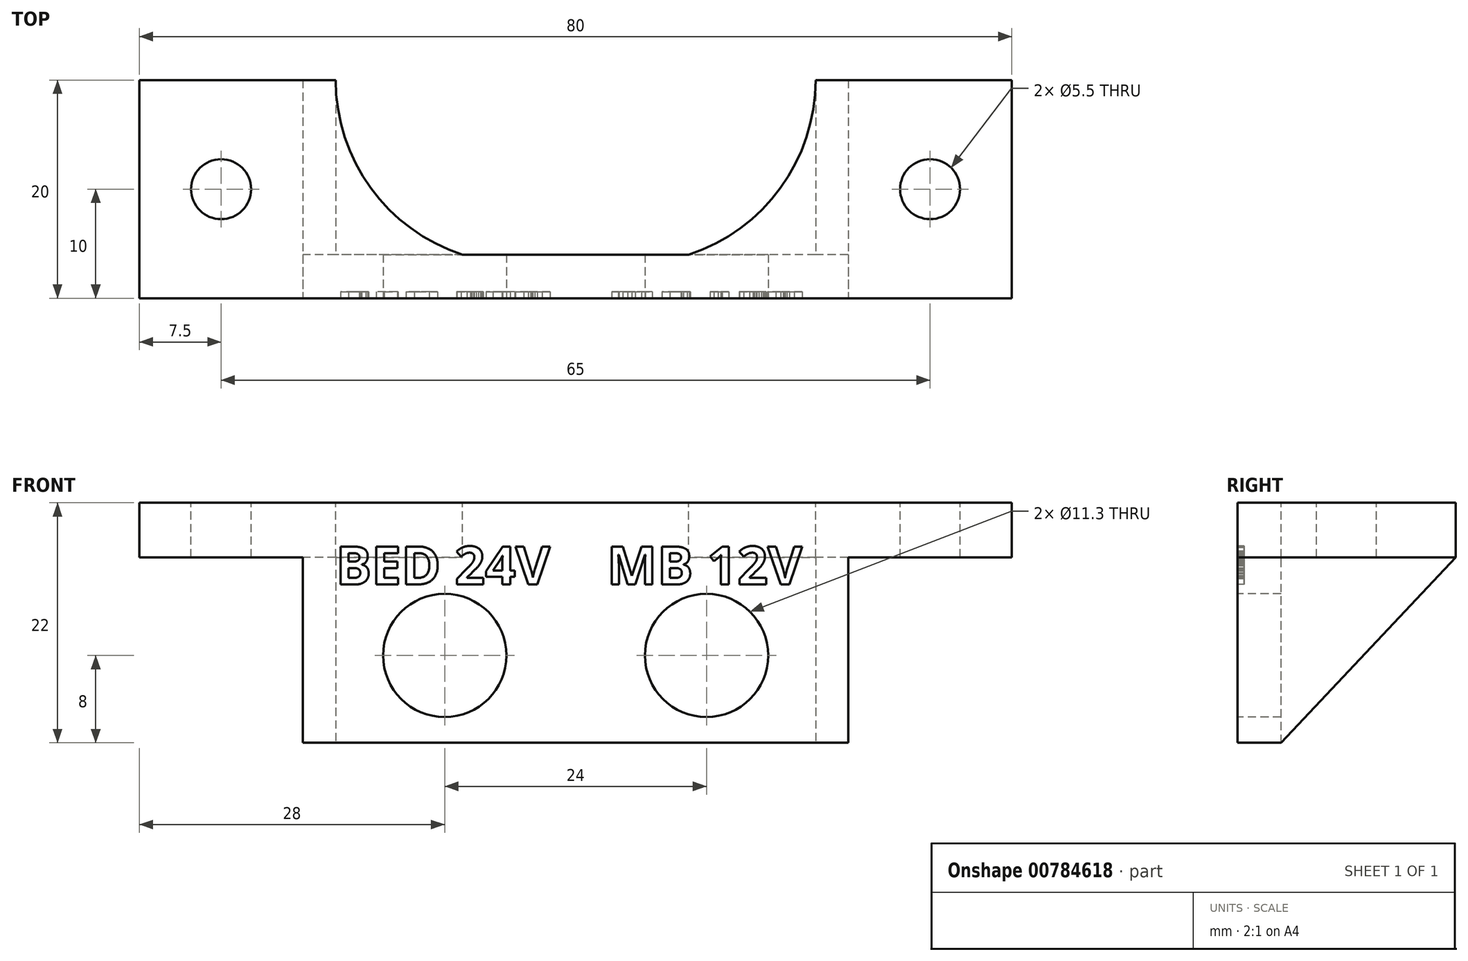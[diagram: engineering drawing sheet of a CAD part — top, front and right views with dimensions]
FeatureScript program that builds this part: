
annotation { "Feature Type Name" : "Feature", "Feature Type Description" : "" }
export const myFeature = defineFeature(function(context is Context, id is Id, definition is map)
    precondition{}
    {
        {
            var Q0;
            Q0=qCreatedBy(makeId("Front.planeOp"),FACE);
            var sketch = newSketch(context, id + "F0", { "sketchPlane" : qUnion([Q0])});
            skLineSegment(sketch, "E0.bottom", {"start": v(25, 11) * mm, "end": v(-25, 11) * mm});
            skLineSegment(sketch, "E0.top", {"start": v(25, -11) * mm, "end": v(-25, -11) * mm});
            skLineSegment(sketch, "E0.left", {"start": v(25, 11) * mm, "end": v(25, -11) * mm});
            skLineSegment(sketch, "E0.right", {"start": v(-25, 11) * mm, "end": v(-25, -11) * mm});
            skPoint(sketch, "E0.middle", {"position": v(0, 0) * mm});
            skCircle(sketch, "E1", {"center": v(-12, -3) * mm, "radius": 5.65 * mm});
            skCircle(sketch, "E2.MirrorC", {"center": v(12, -3) * mm, "radius": 5.65 * mm});
            skSolve(sketch);
        }
        {
            var Q0;
            Q0=qCreatedBy(makeId("Front.planeOp"),FACE);
            var sketch = newSketch(context, id + "F1", { "sketchPlane" : qUnion([Q0])});
            skText(sketch, "E3", { "text": "BED 24V", "fontName": "OpenSans-Bold.ttf"});
            skPoint(sketch, "E4.0", {"position": v(-12, -3) * mm});
            skPoint(sketch, "E5.0", {"position": v(12, -3) * mm});
            skText(sketch, "E6", { "text": "MB 12V", "fontName": "OpenSans-Bold.ttf"});
            const initialGuessF1  = {"E3": [-0.022, 0.0035, 1, 0, 0.00352], "E6": [0.00287, 0.0035, 1, 0, 0.00352]};
            skSetInitialGuess(sketch, initialGuessF1);
            skSolve(sketch);
        }
        {
            var Q0;
            Q0=makeQuery(id+"F0.imprint","IMPRINT",FACE,{"disambiguationData":[TD([[makeQuery(id+"F0.imprint","IMPRINT",EDGE,{"derivedFrom":sQuery(id+"F0.wireOp",EDGE,"E0.bottom")}),1.0]])]});
            extrude(context, id + "F2", {"entities" : qUnion([Q0]), "oppositeDirection" : true, "depth" : 4 * mm, "offsetDistance" : 25 * mm});
        }
        {
            var Q0;
            Q0=makeQuery(id+"F2.opExtrude","SWEPT_FACE",FACE,{"disambiguationData":[OSD([sQuery(id+"F0.wireOp",EDGE,"E0.bottom")])]});
            var sketch = newSketch(context, id + "F3", { "sketchPlane" : qUnion([Q0])});
            skLineSegment(sketch, "E7.bottom", {"start": v(-40, 0) * mm, "end": v(40, 0) * mm});
            skLineSegment(sketch, "E7.top", {"start": v(-40, 20) * mm, "end": v(40, 20) * mm});
            skLineSegment(sketch, "E7.left", {"start": v(-40, 0) * mm, "end": v(-40, 20) * mm});
            skLineSegment(sketch, "E7.right", {"start": v(40, 0) * mm, "end": v(40, 20) * mm});
            skPoint(sketch, "E7.middle", {"position": v(0, 10) * mm});
            skLineSegment(sketch, "E8", {"start": v(-25, 0) * mm, "end": v(-25, 20) * mm});
            skLineSegment(sketch, "E9", {"start": v(-22, 20) * mm, "end": v(-22, 4) * mm});
            skLineSegment(sketch, "E10.MirrorCS", {"start": v(22, 20) * mm, "end": v(22, 4) * mm});
            skLineSegment(sketch, "E11.MirrorCS", {"start": v(25, 0) * mm, "end": v(25, 20) * mm});
            skArc(sketch, "E12", {"start": v(-22, 20) * mm, "mid": v(-15.07, 6.4) * mm, "end": v(0, 4) * mm});
            skArc(sketch, "E13.MirrorCS", {"start": v(22, 20) * mm, "mid": v(15.07, 6.4) * mm, "end": v(0, 4) * mm});
            skCircle(sketch, "E14", {"center": v(-32.5, 10) * mm, "radius": 2.75 * mm});
            skPoint(sketch, "E14.centerSnap0", {"position": v(-40, 10) * mm});
            skCircle(sketch, "E15.MirrorC", {"center": v(32.5, 10) * mm, "radius": 2.75 * mm});
            skSolve(sketch);
        }
        {
            var Q0;
            {var subQ0=sQuery(id+"F3.wireOp",EDGE,"E7.left");Q0=makeQuery(id+"F3.imprint","IMPRINT",FACE,{"disambiguationData":[TD([[makeQuery(id+"F3.imprint","IMPRINT",EDGE,{"derivedFrom":subQ0}),-1.0]])]});}
            var Q1;
            {var subQ4=sQuery(id+"F3.wireOp",EDGE,"E7.right");Q1=makeQuery(id+"F3.imprint","IMPRINT",FACE,{"disambiguationData":[TD([[makeQuery(id+"F3.imprint","IMPRINT",EDGE,{"derivedFrom":subQ4}),1.0]])]});}
            var Q2;
            {var subQ0=sQuery(id+"F3.wireOp",EDGE,"E9");Q2=makeQuery(id+"F3.imprint","IMPRINT",FACE,{"disambiguationData":[TD([[makeQuery(id+"F3.imprint","IMPRINT",EDGE,{"derivedFrom":subQ0}),-1.0]])]});}
            var Q3;
            {var subQ0=sQuery(id+"F3.wireOp",EDGE,"E10.MirrorCS");Q3=makeQuery(id+"F3.imprint","IMPRINT",FACE,{"disambiguationData":[TD([[makeQuery(id+"F3.imprint","IMPRINT",EDGE,{"derivedFrom":subQ0}),1.0]])]});}
            var Q4;
            {var subQ0=sQuery(id+"F3.wireOp",EDGE,"E9");Q4=makeQuery(id+"F3.imprint","IMPRINT",FACE,{"disambiguationData":[TD([[makeQuery(id+"F3.imprint","IMPRINT",EDGE,{"derivedFrom":subQ0}),1.0]])]});}
            var Q5;
            {var subQ0=sQuery(id+"F3.wireOp",EDGE,"E10.MirrorCS");Q5=makeQuery(id+"F3.imprint","IMPRINT",FACE,{"disambiguationData":[TD([[makeQuery(id+"F3.imprint","IMPRINT",EDGE,{"derivedFrom":subQ0}),-1.0]])]});}
            extrude(context, id + "F4", {"entities" : qUnion([Q0, Q1, Q2, Q3, Q4, Q5]), "operationType" : NewBodyOperationType.ADD, "oppositeDirection" : true, "depth" : 5 * mm, "offsetDistance" : 25 * mm});
        }
        {
            var Q0;
            {var subQ0=sQuery(id+"F3.wireOp",EDGE,"E9");Q0=makeQuery(id+"F3.imprint","IMPRINT",FACE,{"disambiguationData":[TD([[makeQuery(id+"F3.imprint","IMPRINT",EDGE,{"derivedFrom":subQ0}),-1.0]])]});}
            var Q1;
            {var subQ0=sQuery(id+"F3.wireOp",EDGE,"E10.MirrorCS");Q1=makeQuery(id+"F3.imprint","IMPRINT",FACE,{"disambiguationData":[TD([[makeQuery(id+"F3.imprint","IMPRINT",EDGE,{"derivedFrom":subQ0}),1.0]])]});}
            var Q2;
            Q2=makeQuery(id+"F2.opExtrude","SWEPT_FACE",FACE,{"disambiguationData":[OSD([sQuery(id+"F0.wireOp",EDGE,"E0.top")])]});
            extrude(context, id + "F5", {"entities" : qUnion([Q0, Q1]), "operationType" : NewBodyOperationType.ADD, "endBound" : BoundingType.UP_TO_SURFACE, "oppositeDirection" : true, "depth" : 25 * mm, "endBoundEntityFace" : qUnion([Q2]), "offsetDistance" : 25 * mm});
        }
        {
            var Q0;
            Q0=makeQuery(id+"F5.boolean.opBoolean","MERGE",FACE,{"derivedFrom":[makeQuery(id+"F2.opExtrude","SWEPT_FACE",FACE,{"disambiguationData":[OSD([sQuery(id+"F0.wireOp",EDGE,"E0.right")])]}),makeQuery(id+"F5.opExtrude","SWEPT_FACE",FACE,{"disambiguationData":[OSD([sQuery(id+"F3.wireOp",EDGE,"E8")])]})]});
            var sketch = newSketch(context, id + "F6", { "sketchPlane" : qUnion([Q0])});
            skPoint(sketch, "E16.0", {"position": v(-4, -11) * mm});
            skLineSegment(sketch, "E17", {"start": v(-20, 6) * mm, "end": v(-4, -11) * mm});
            skSolve(sketch);
        }
        {
            var Q0;
            {var subQ0=sQuery(id+"F6.wireOp",EDGE,"E17");Q0=makeQuery(id+"F6.imprint","IMPRINT",FACE,{"disambiguationData":[TD([[makeQuery(id+"F6.imprint","IMPRINT",EDGE,{"derivedFrom":subQ0}),-1.0]])]});}
            extrude(context, id + "F7", {"entities" : qUnion([Q0]), "operationType" : NewBodyOperationType.REMOVE, "endBound" : BoundingType.THROUGH_ALL, "oppositeDirection" : true, "depth" : 25 * mm, "offsetDistance" : 25 * mm});
        }
        {
            var Q0;
            Q0 = qSketchRegion(id + "F1", true);
            extrude(context, id + "F8", {"entities" : qUnion([Q0]), "operationType" : NewBodyOperationType.REMOVE, "oppositeDirection" : true, "depth" : 0.6 * mm, "offsetDistance" : 25 * mm});
        }
    });
